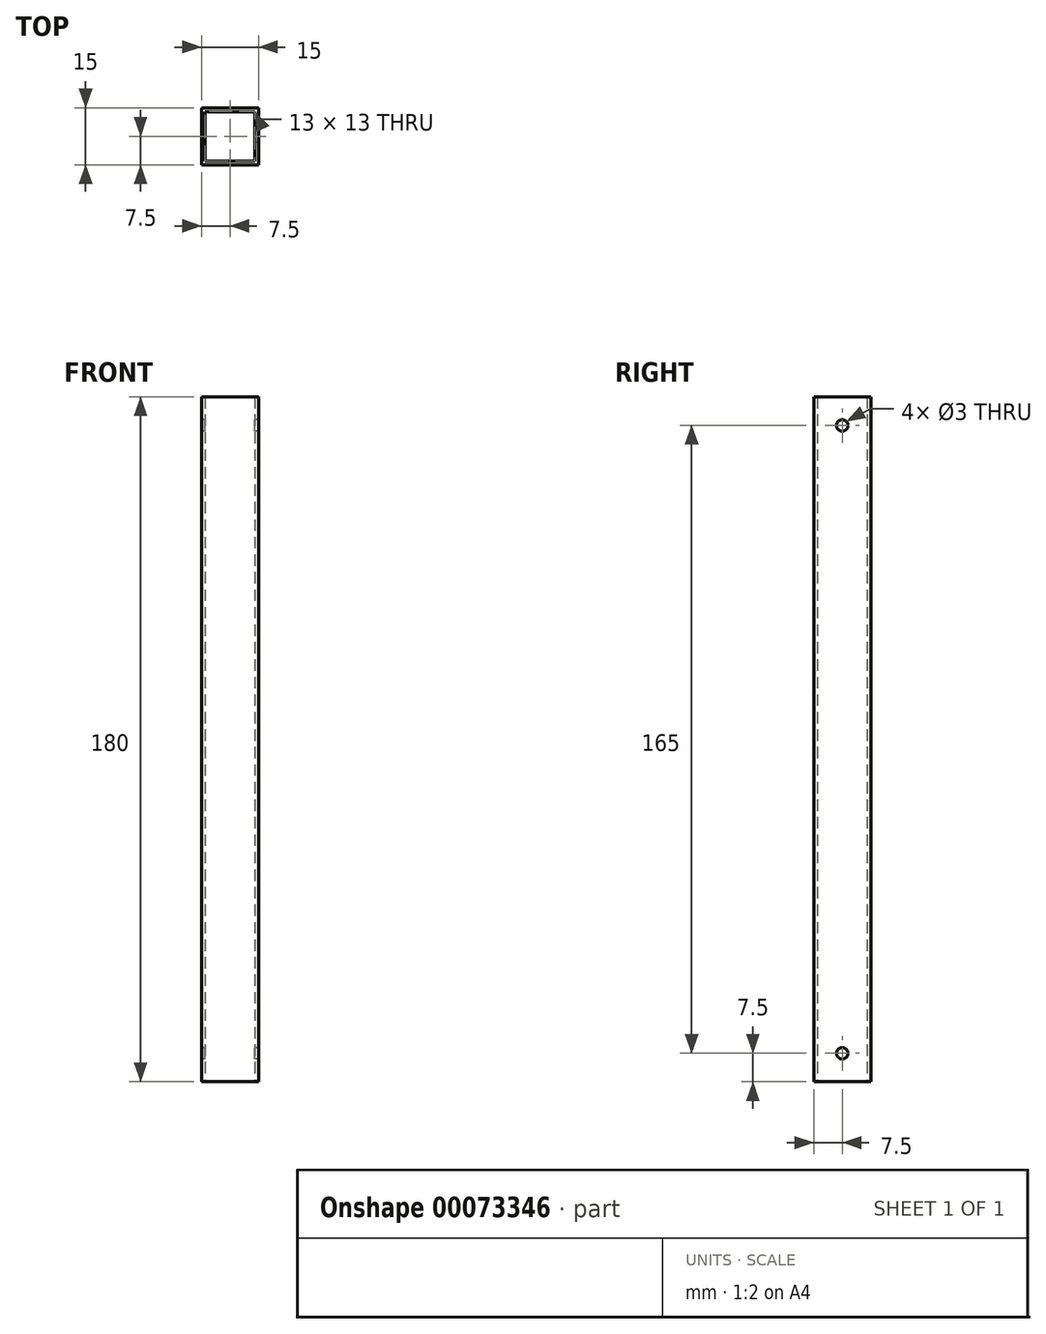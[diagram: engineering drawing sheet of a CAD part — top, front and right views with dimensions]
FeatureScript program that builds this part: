
annotation { "Feature Type Name" : "Feature", "Feature Type Description" : "" }
export const myFeature = defineFeature(function(context is Context, id is Id, definition is map)
    precondition{}
    {
        {
            var Q0;
            Q0=qCreatedBy(makeId("Top.planeOp"),FACE);
            var sketch = newSketch(context, id + "F0", { "sketchPlane" : qUnion([Q0])});
            skLineSegment(sketch, "E0.bottom", {"start": v(-7.5, 7.5) * mm, "end": v(7.5, 7.5) * mm});
            skLineSegment(sketch, "E0.top", {"start": v(-7.5, -7.5) * mm, "end": v(7.5, -7.5) * mm});
            skLineSegment(sketch, "E0.left", {"start": v(-7.5, 7.5) * mm, "end": v(-7.5, -7.5) * mm});
            skLineSegment(sketch, "E0.right", {"start": v(7.5, 7.5) * mm, "end": v(7.5, -7.5) * mm});
            skLineSegment(sketch, "E1.bottom", {"start": v(-6.5, 6.5) * mm, "end": v(6.5, 6.5) * mm});
            skLineSegment(sketch, "E1.top", {"start": v(-6.5, -6.5) * mm, "end": v(6.5, -6.5) * mm});
            skLineSegment(sketch, "E1.left", {"start": v(-6.5, 6.5) * mm, "end": v(-6.5, -6.5) * mm});
            skLineSegment(sketch, "E1.right", {"start": v(6.5, 6.5) * mm, "end": v(6.5, -6.5) * mm});
            skLineSegment(sketch, "E2", {"start": v(-7.5, 7.5) * mm, "end": v(-6.5, 6.5) * mm});
            skLineSegment(sketch, "E3", {"start": v(6.5, -6.5) * mm, "end": v(7.5, -7.5) * mm});
            skLineSegment(sketch, "E4", {"start": v(-6.5, 6.5) * mm, "end": v(6.5, -6.5) * mm});
            skPoint(sketch, "E5", {"position": v(0, 0) * mm});
            skSolve(sketch);
        }
        {
            var Q0;
            Q0=makeQuery(id+"F0.imprint","IMPRINT",FACE,{"disambiguationData":[TD([[makeQuery(id+"F0.imprint","IMPRINT",EDGE,{"derivedFrom":sQuery(id+"F0.wireOp",EDGE,"E0.top")}),1.0]])]});
            var Q1;
            Q1=makeQuery(id+"F0.imprint","IMPRINT",FACE,{"disambiguationData":[TD([[makeQuery(id+"F0.imprint","IMPRINT",EDGE,{"derivedFrom":sQuery(id+"F0.wireOp",EDGE,"E0.bottom")}),-1.0]])]});
            extrude(context, id + "F1", {"entities" : qUnion([Q0, Q1]), "depth" : 180 * mm, "symmetric" : true});
        }
        {
            var Q0;
            Q0=makeQuery(id+"F1.opExtrude","SWEPT_FACE",FACE,{"disambiguationData":[OSD([sQuery(id+"F0.wireOp",EDGE,"E0.left")])]});
            var sketch = newSketch(context, id + "F2", { "sketchPlane" : qUnion([Q0])});
            skLineSegment(sketch, "E6.bottom", {"start": v(-7.5, 90) * mm, "end": v(7.5, 90) * mm});
            skLineSegment(sketch, "E6.top", {"start": v(-7.5, 75) * mm, "end": v(7.5, 75) * mm});
            skLineSegment(sketch, "E6.left", {"start": v(-7.5, 90) * mm, "end": v(-7.5, 75) * mm});
            skLineSegment(sketch, "E6.right", {"start": v(7.5, 90) * mm, "end": v(7.5, 75) * mm});
            skLineSegment(sketch, "E7.bottom", {"start": v(-7.5, -90) * mm, "end": v(7.5, -90) * mm});
            skLineSegment(sketch, "E7.top", {"start": v(-7.5, -75) * mm, "end": v(7.5, -75) * mm});
            skLineSegment(sketch, "E7.left", {"start": v(-7.5, -90) * mm, "end": v(-7.5, -75) * mm});
            skLineSegment(sketch, "E7.right", {"start": v(7.5, -90) * mm, "end": v(7.5, -75) * mm});
            skLineSegment(sketch, "E8", {"start": v(-7.5, 90) * mm, "end": v(7.5, 75) * mm});
            skLineSegment(sketch, "E9", {"start": v(-7.5, -75) * mm, "end": v(7.5, -90) * mm});
            skPoint(sketch, "E10", {"position": v(0, -82.5) * mm});
            skPoint(sketch, "E11", {"position": v(0, 82.5) * mm});
            skSolve(sketch);
        }
        {
            var Q0;
            Q0=sQuery(id+"F2.wireOp",VERTEX,"E11");
            var Q1;
            Q1=sQuery(id+"F2.wireOp",VERTEX,"E10");
            var Q2;
            Q2=makeQuery(id+"F1.opExtrude","SWEPT_BODY",BODY,{"disambiguationData":[OSD([sQuery(id+"F0.wireOp",EDGE,"E0.bottom"),sQuery(id+"F0.wireOp",EDGE,"E0.top"),sQuery(id+"F0.wireOp",EDGE,"E0.left"),sQuery(id+"F0.wireOp",EDGE,"E0.right"),sQuery(id+"F0.wireOp",EDGE,"E1.bottom"),sQuery(id+"F0.wireOp",EDGE,"E1.top"),sQuery(id+"F0.wireOp",EDGE,"E1.left"),sQuery(id+"F0.wireOp",EDGE,"E1.right")])]});
            hole(context, id + "F3", {"style" : HoleStyle.SIMPLE, "holeDiameter" : 3 * mm, "endStyle" : HoleEndStyle.THROUGH, "locations" : qUnion([Q0, Q1]), "scope" : qUnion([Q2])});
        }
    });
